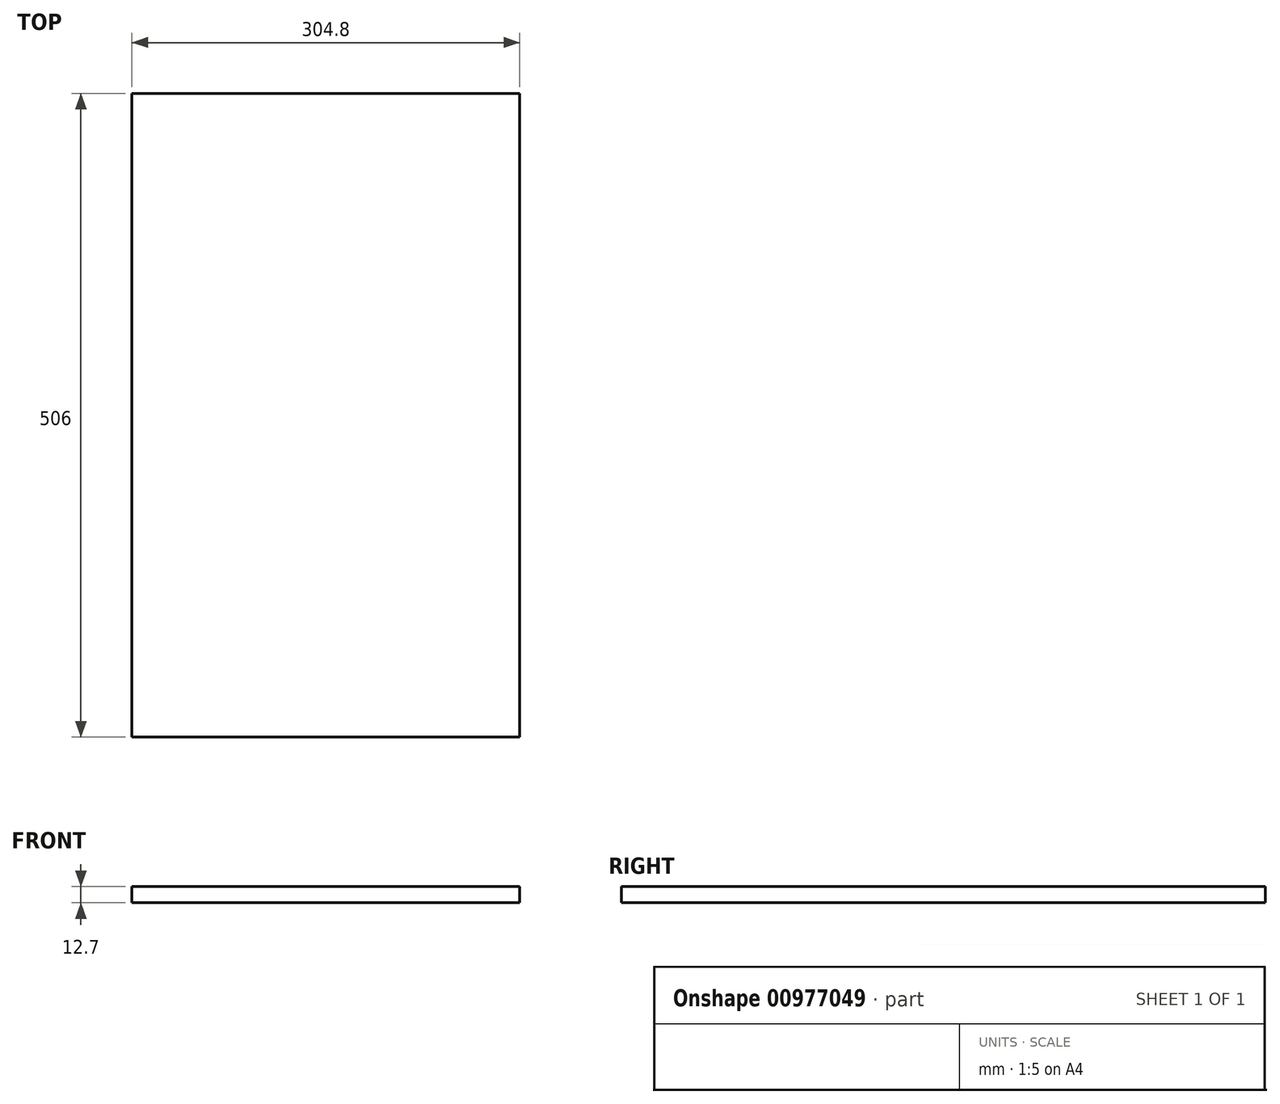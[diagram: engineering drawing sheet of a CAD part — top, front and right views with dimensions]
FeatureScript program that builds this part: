
annotation { "Feature Type Name" : "Feature", "Feature Type Description" : "" }
export const myFeature = defineFeature(function(context is Context, id is Id, definition is map)
    precondition{}
    {
        {
            var Q0;
            Q0=qCreatedBy(makeId("Front.planeOp"),FACE);
            var sketch = newSketch(context, id + "F0", { "sketchPlane" : qUnion([Q0])});
            skLineSegment(sketch, "E0.bottom", {"start": v(152.4, -6.35) * mm, "end": v(-152.4, -6.35) * mm});
            skLineSegment(sketch, "E0.top", {"start": v(152.4, 6.35) * mm, "end": v(-152.4, 6.35) * mm});
            skLineSegment(sketch, "E0.left", {"start": v(152.4, -6.35) * mm, "end": v(152.4, 6.35) * mm});
            skLineSegment(sketch, "E0.right", {"start": v(-152.4, -6.35) * mm, "end": v(-152.4, 6.35) * mm});
            skPoint(sketch, "E0.middle", {"position": v(0, 0) * mm});
            skSolve(sketch);
        }
        {
            var Q0;
            Q0 = qSketchRegion(id + "F0", true);
            extrude(context, id + "F1", {"entities" : qUnion([Q0]), "endBound" : BoundingType.SYMMETRIC, "depth" : 506 * mm, "offsetDistance" : 25.4 * mm});
        }
    });
